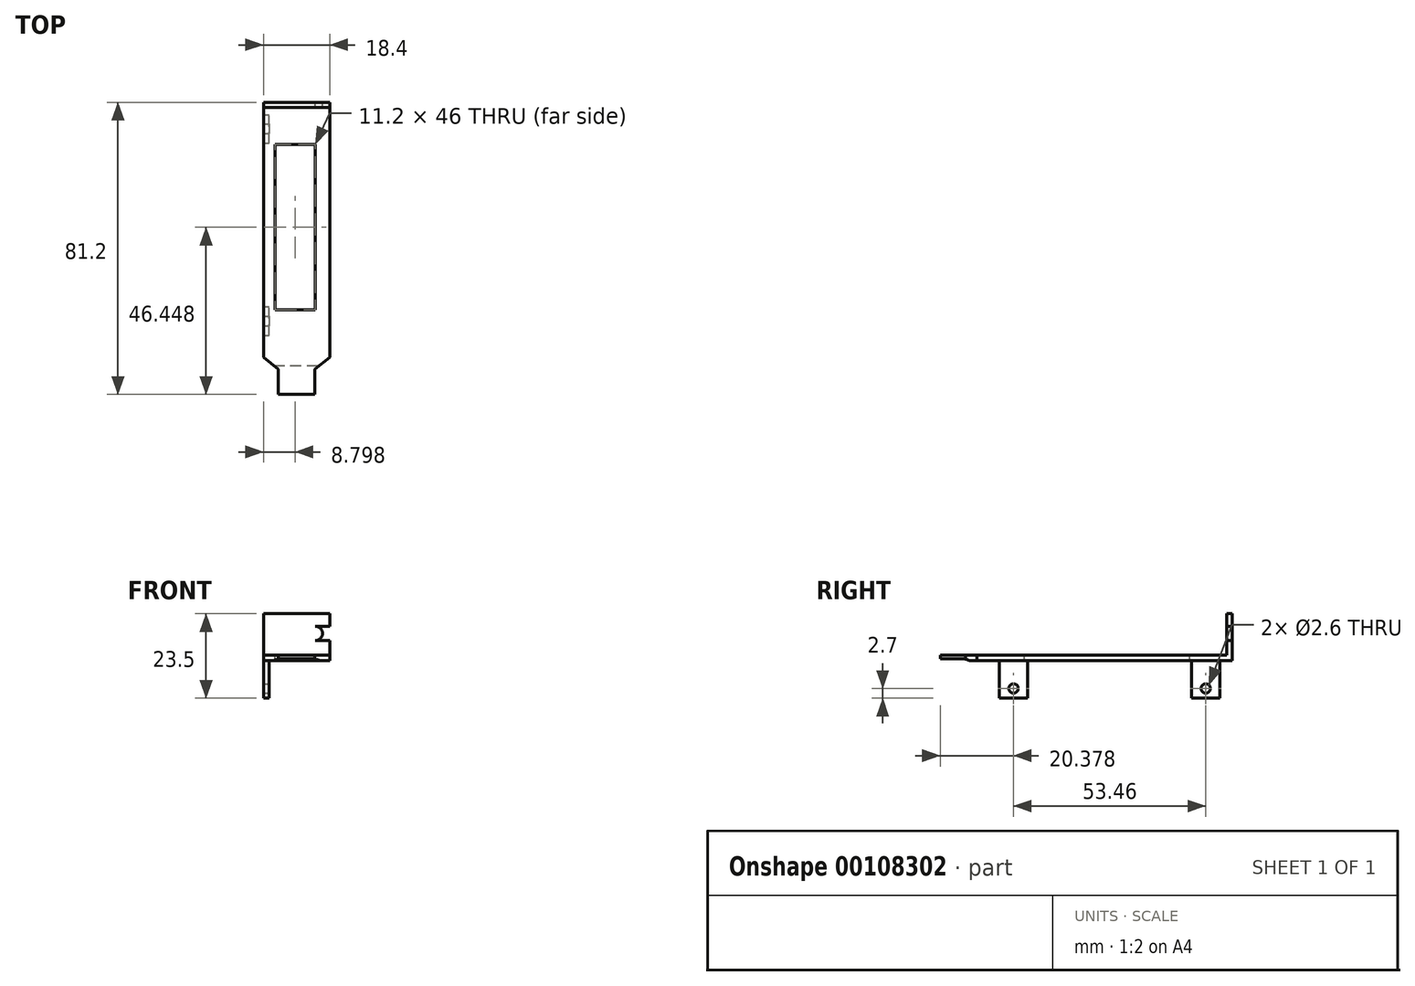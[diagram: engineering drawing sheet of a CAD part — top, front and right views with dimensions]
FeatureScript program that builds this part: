
annotation { "Feature Type Name" : "Feature", "Feature Type Description" : "" }
export const myFeature = defineFeature(function(context is Context, id is Id, definition is map)
    precondition{}
    {
        {
            var Q0;
            Q0=qCreatedBy(makeId("Top.planeOp"),FACE);
            var sketch = newSketch(context, id + "F0", { "sketchPlane" : qUnion([Q0])});
            skLineSegment(sketch, "E0.bottom", {"start": v(-5.44, 44.64) * mm, "end": v(12.96, 44.64) * mm});
            skLineSegment(sketch, "E0.left", {"start": v(-5.44, 44.64) * mm, "end": v(-5.44, -26.3) * mm});
            skLineSegment(sketch, "E0.right", {"start": v(12.96, 44.64) * mm, "end": v(12.96, -26.3) * mm});
            skPoint(sketch, "E0.middle", {"position": v(0, 0) * mm});
            skLineSegment(sketch, "E1", {"start": v(-1.34, -29.56) * mm, "end": v(-5.44, -26.3) * mm});
            skLineSegment(sketch, "E2", {"start": v(12.96, -26.3) * mm, "end": v(8.86, -29.56) * mm});
            skLineSegment(sketch, "E3", {"start": v(-1.34, -29.56) * mm, "end": v(8.86, -29.56) * mm});
            skLineSegment(sketch, "E4", {"start": v(-1.34, -29.56) * mm, "end": v(-1.34, -36.56) * mm});
            skLineSegment(sketch, "E5", {"start": v(-1.34, -36.56) * mm, "end": v(8.86, -36.56) * mm});
            skLineSegment(sketch, "E6", {"start": v(8.86, -36.56) * mm, "end": v(8.86, -29.56) * mm});
            skPoint(sketch, "E7.middle", {"position": v(4.18, 5.9) * mm});
            skSolve(sketch);
        }
        {
            var Q0;
            Q0 = qSketchRegion(id + "F0", true);
            extrude(context, id + "F1", {"entities" : qUnion([Q0]), "depth" : 1.5 * mm});
        }
        {
            var Q0;
            Q0=makeQuery(id+"F1.opExtrude","CAP_FACE",FACE,{"disambiguationData":[OSD([sQuery(id+"F0.wireOp",EDGE,"E0.bottom"),sQuery(id+"F0.wireOp",EDGE,"E0.left"),sQuery(id+"F0.wireOp",EDGE,"E0.right"),sQuery(id+"F0.wireOp",EDGE,"E1"),sQuery(id+"F0.wireOp",EDGE,"E2"),sQuery(id+"F0.wireOp",EDGE,"E4"),sQuery(id+"F0.wireOp",EDGE,"E5"),sQuery(id+"F0.wireOp",EDGE,"E6")])],"isStart":false});
            var sketch = newSketch(context, id + "F2", { "sketchPlane" : qUnion([Q0])});
            skLineSegment(sketch, "E8", {"start": v(-2.24, 32.89) * mm, "end": v(-2.24, -13.11) * mm});
            skLineSegment(sketch, "E9", {"start": v(-2.24, -13.11) * mm, "end": v(8.96, -13.11) * mm});
            skLineSegment(sketch, "E10", {"start": v(8.96, -13.11) * mm, "end": v(8.96, 32.89) * mm});
            skLineSegment(sketch, "E11", {"start": v(8.96, 32.89) * mm, "end": v(-2.24, 32.89) * mm});
            skLineSegment(sketch, "E12.0", {"start": v(-5.44, 44.64) * mm, "end": v(-5.44, -26.3) * mm});
            skSolve(sketch);
        }
        {
            var Q0;
            Q0=makeQuery(id+"F2.imprint","IMPRINT",FACE,{"disambiguationData":[TD([[makeQuery(id+"F2.imprint","IMPRINT",EDGE,{"derivedFrom":sQuery(id+"F2.wireOp",EDGE,"E8")}),1.0]])]});
            extrude(context, id + "F3", {"entities" : qUnion([Q0]), "operationType" : NewBodyOperationType.REMOVE, "oppositeDirection" : true, "depth" : 25 * mm});
        }
        {
            var Q0;
            Q0=makeQuery(id+"F1.opExtrude","CAP_FACE",FACE,{"disambiguationData":[OSD([sQuery(id+"F0.wireOp",EDGE,"E0.bottom"),sQuery(id+"F0.wireOp",EDGE,"E0.left"),sQuery(id+"F0.wireOp",EDGE,"E0.right"),sQuery(id+"F0.wireOp",EDGE,"E1"),sQuery(id+"F0.wireOp",EDGE,"E2"),sQuery(id+"F0.wireOp",EDGE,"E4"),sQuery(id+"F0.wireOp",EDGE,"E5"),sQuery(id+"F0.wireOp",EDGE,"E6")])],"isStart":true});
            var sketch = newSketch(context, id + "F4", { "sketchPlane" : qUnion([Q0])});
            skLineSegment(sketch, "E13", {"start": v(-3.94, 26.3) * mm, "end": v(-3.94, -44.64) * mm});
            skLineSegment(sketch, "E14", {"start": v(-3.94, 26.3) * mm, "end": v(-5.44, 26.3) * mm});
            skPoint(sketch, "E15.0", {"position": v(-5.44, -44.64) * mm});
            skLineSegment(sketch, "E16.0", {"start": v(-5.44, -44.64) * mm, "end": v(-5.44, 26.3) * mm});
            skLineSegment(sketch, "E17", {"start": v(-3.94, -44.64) * mm, "end": v(-5.44, -44.64) * mm});
            skLineSegment(sketch, "E18", {"start": v(-5.44, 26.3) * mm, "end": v(-3.94, 26.3) * mm});
            skSolve(sketch);
        }
        {
            var Q0;
            Q0=makeQuery(id+"F4.imprint","IMPRINT",FACE,{"disambiguationData":[TD([[makeQuery(id+"F4.imprint","IMPRINT",EDGE,{"derivedFrom":sQuery(id+"F4.wireOp",EDGE,"E13")}),-1.0]])]});
            extrude(context, id + "F5", {"entities" : qUnion([Q0]), "operationType" : NewBodyOperationType.ADD, "depth" : 10.5 * mm});
        }
        {
            var Q0;
            Q0=makeQuery(id+"F5.opExtrude","SWEPT_FACE",FACE,{"disambiguationData":[OSD([sQuery(id+"F4.wireOp",EDGE,"E13")])]});
            var sketch = newSketch(context, id + "F6", { "sketchPlane" : qUnion([Q0])});
            skCircle(sketch, "E19", {"center": v(-16.18, -7.8) * mm, "radius": 1.3 * mm});
            skCircle(sketch, "E20", {"center": v(37.28, -7.8) * mm, "radius": 1.3 * mm});
            skLineSegment(sketch, "E21", {"start": v(-16.18, -7.8) * mm, "end": v(37.28, -7.8) * mm, "construction": true});
            skLineSegment(sketch, "E22", {"start": v(-20.15, -10.5) * mm, "end": v(-20.15, 0) * mm});
            skLineSegment(sketch, "E23", {"start": v(-20.15, -10.5) * mm, "end": v(-12.21, -10.5) * mm});
            skLineSegment(sketch, "E24", {"start": v(-12.21, 0) * mm, "end": v(-12.21, -10.5) * mm});
            skLineSegment(sketch, "E25", {"start": v(33.3, -10.5) * mm, "end": v(33.3, 0) * mm});
            skLineSegment(sketch, "E26", {"start": v(33.3, -10.5) * mm, "end": v(41.2, -10.5) * mm});
            skLineSegment(sketch, "E27", {"start": v(41.2, 0) * mm, "end": v(41.2, -10.5) * mm});
            skSolve(sketch);
        }
        {
            var Q0;
            {var subQ0=sQuery(id+"F6.wireOp",EDGE,"E24");Q0=makeQuery(id+"F6.imprint","IMPRINT",FACE,{"disambiguationData":[TD([[makeQuery(id+"F6.imprint","IMPRINT",EDGE,{"derivedFrom":subQ0}),1.0]])]});}
            var Q1;
            Q1=makeQuery(id+"F6.imprint","IMPRINT",FACE,{"disambiguationData":[TD([[makeQuery(id+"F6.imprint","IMPRINT",EDGE,{"derivedFrom":sQuery(id+"F6.wireOp",EDGE,"E19")}),1.0]])]});
            var Q2;
            Q2=makeQuery(id+"F6.imprint","IMPRINT",FACE,{"disambiguationData":[TD([[makeQuery(id+"F6.imprint","IMPRINT",EDGE,{"derivedFrom":sQuery(id+"F6.wireOp",EDGE,"E20")}),1.0]])]});
            var Q3;
            {var subQ3=sQuery(id+"F6.wireOp",EDGE,"E27");Q3=makeQuery(id+"F6.imprint","IMPRINT",FACE,{"disambiguationData":[TD([[makeQuery(id+"F6.imprint","IMPRINT",EDGE,{"derivedFrom":subQ3}),1.0]])]});}
            var Q4;
            {var subQ0=sQuery(id+"F6.wireOp",EDGE,"E22");Q4=makeQuery(id+"F6.imprint","IMPRINT",FACE,{"disambiguationData":[TD([[makeQuery(id+"F6.imprint","IMPRINT",EDGE,{"derivedFrom":subQ0}),1.0]])]});}
            extrude(context, id + "F7", {"entities" : qUnion([Q0, Q1, Q2, Q3, Q4]), "operationType" : NewBodyOperationType.REMOVE, "oppositeDirection" : true, "depth" : 25 * mm});
        }
        {
            var Q0;
            {var subQ0=sQuery(id+"F4.wireOp",EDGE,"E13");var subQ1=makeQuery(id+"F5.opExtrude","CAP_EDGE",EDGE,{"disambiguationData":[OSD([subQ0])],"isStart":true});var subQ2=sQuery(id+"F0.wireOp",EDGE,"E0.bottom");Q0=makeQuery(id+"F7.boolean.opBoolean","MERGE",FACE,{"derivedFrom":[makeQuery(id+"F1.opExtrude","CAP_FACE",FACE,{"disambiguationData":[OSD([subQ2,sQuery(id+"F0.wireOp",EDGE,"E0.left"),sQuery(id+"F0.wireOp",EDGE,"E0.right"),sQuery(id+"F0.wireOp",EDGE,"E1"),sQuery(id+"F0.wireOp",EDGE,"E2"),sQuery(id+"F0.wireOp",EDGE,"E4"),sQuery(id+"F0.wireOp",EDGE,"E5"),sQuery(id+"F0.wireOp",EDGE,"E6")])],"isStart":true}),makeQuery(id+"F7.opExtrude","SWEPT_FACE",FACE,{"disambiguationData":[OSD([subQ0]),TDD([makeQuery(id+"F6.imprint","IMPRINT",EDGE,{"disambiguationData":[TD([[makeQuery(id+"F6.imprint","INTERSECT",VERTEX,{"derivedFrom":[subQ1,sQuery(id+"F6.wireOp",EDGE,"E22")]}),1.0]])],"derivedFrom":subQ1})])]}),makeQuery(id+"F7.opExtrude","SWEPT_FACE",FACE,{"disambiguationData":[OSD([subQ0]),TDD([makeQuery(id+"F6.imprint","IMPRINT",EDGE,{"disambiguationData":[TD([[makeQuery(id+"F6.imprint","INTERSECT",VERTEX,{"derivedFrom":[subQ1,sQuery(id+"F6.wireOp",EDGE,"E27")]}),-1.0]])],"derivedFrom":subQ1})])]}),makeQuery(id+"F7.opExtrude","SWEPT_FACE",FACE,{"disambiguationData":[OSD([subQ0]),TDD([makeQuery(id+"F6.imprint","IMPRINT",EDGE,{"disambiguationData":[TD([[makeQuery(id+"F6.imprint","INTERSECT",VERTEX,{"derivedFrom":[subQ1,sQuery(id+"F6.wireOp",EDGE,"E24")]}),-1.0]])],"derivedFrom":subQ1})])]})]});}
            var sketch = newSketch(context, id + "F8", { "sketchPlane" : qUnion([Q0])});
            skLineSegment(sketch, "E28", {"start": v(-2.6, 28.56) * mm, "end": v(10.11, 28.56) * mm});
            skSolve(sketch);
        }
        {
            var Q0;
            {var subQ0=sQuery(id+"F8.wireOp",EDGE,"E28");Q0=makeQuery(id+"F8.imprint","IMPRINT",FACE,{"disambiguationData":[TD([[makeQuery(id+"F8.imprint","IMPRINT",EDGE,{"derivedFrom":subQ0}),1.0]])]});}
            extrude(context, id + "F9", {"entities" : qUnion([Q0]), "operationType" : NewBodyOperationType.REMOVE, "oppositeDirection" : true, "depth" : .50 * mm});
        }
        {
            var Q0;
            Q0=makeQuery(id+"F9.boolean.opBoolean","COPY",EDGE,{"derivedFrom":makeQuery(id+"F9.opExtrude","CAP_EDGE",EDGE,{"disambiguationData":[OSD([sQuery(id+"F8.wireOp",EDGE,"E28")])],"isStart":false})});
            fillet(context, id + "F10", {"entities" : qUnion([Q0]), "radius" : 5 * mm, "tangentPropagation" : true, "allowEdgeOverflow" : false});
        }
        {
            var Q0;
            Q0=makeQuery(id+"F1.opExtrude","CAP_FACE",FACE,{"disambiguationData":[OSD([sQuery(id+"F0.wireOp",EDGE,"E0.bottom"),sQuery(id+"F0.wireOp",EDGE,"E0.left"),sQuery(id+"F0.wireOp",EDGE,"E0.right"),sQuery(id+"F0.wireOp",EDGE,"E1"),sQuery(id+"F0.wireOp",EDGE,"E2"),sQuery(id+"F0.wireOp",EDGE,"E4"),sQuery(id+"F0.wireOp",EDGE,"E5"),sQuery(id+"F0.wireOp",EDGE,"E6")])],"isStart":false});
            var sketch = newSketch(context, id + "F11", { "sketchPlane" : qUnion([Q0])});
            skLineSegment(sketch, "E29", {"start": v(-5.44, 43.14) * mm, "end": v(12.96, 43.14) * mm});
            skSolve(sketch);
        }
        {
            var Q0;
            {var subQ0=sQuery(id+"F11.wireOp",EDGE,"E29");Q0=makeQuery(id+"F11.imprint","IMPRINT",FACE,{"disambiguationData":[TD([[makeQuery(id+"F11.imprint","IMPRINT",EDGE,{"derivedFrom":subQ0}),1.0]])]});}
            extrude(context, id + "F12", {"entities" : qUnion([Q0]), "operationType" : NewBodyOperationType.ADD, "depth" : 11.5 * mm});
        }
        {
            var Q0;
            {var subQ0=sQuery(id+"F0.wireOp",EDGE,"E0.bottom");Q0=makeQuery(id+"F12.boolean.opBoolean","MERGE",FACE,{"derivedFrom":[makeQuery(id+"F1.opExtrude","SWEPT_FACE",FACE,{"disambiguationData":[OSD([subQ0])]}),makeQuery(id+"F12.opExtrude","SWEPT_FACE",FACE,{"disambiguationData":[OSD([subQ0])]})]});}
            var sketch = newSketch(context, id + "F13", { "sketchPlane" : qUnion([Q0])});
            skLineSegment(sketch, "E30.0", {"start": v(5.44, 13) * mm, "end": v(5.44, 0) * mm});
            skLineSegment(sketch, "E30.1", {"start": v(5.44, 0) * mm, "end": v(-12.96, 0) * mm});
            skLineSegment(sketch, "E31.0", {"start": v(5.44, 13) * mm, "end": v(-12.96, 13) * mm});
            skLineSegment(sketch, "E32.0", {"start": v(5.44, 1.5) * mm, "end": v(-12.96, 1.5) * mm});
            skLineSegment(sketch, "E33", {"start": v(-3.76, 0) * mm, "end": v(-3.76, 13) * mm, "construction": true});
            skLineSegment(sketch, "E34.MirrorCS", {"start": v(-8.96, 5.5) * mm, "end": v(-12.96, 5.5) * mm});
            skLineSegment(sketch, "E35.MirrorCS", {"start": v(-8.96, 9.5) * mm, "end": v(-12.96, 9.5) * mm});
            skCircle(sketch, "E36.MirrorC", {"center": v(-8.96, 7.5) * mm, "radius": 2 * mm});
            skSolve(sketch);
        }
        {
            var Q0;
            {var subQ0=sQuery(id+"F13.wireOp",EDGE,"E36.MirrorC");var subQ1=makeQuery(id+"F13.imprint","INTERSECT",VERTEX,{"derivedFrom":[sQuery(id+"F13.wireOp",EDGE,"E34.MirrorCS"),subQ0]});Q0=makeQuery(id+"F13.imprint","IMPRINT",FACE,{"disambiguationData":[TD([[makeQuery(id+"F13.imprint","IMPRINT",EDGE,{"disambiguationData":[TD([[subQ1,1.0]])],"derivedFrom":subQ0}),-1.0]])]});}
            var Q1;
            {var subQ0=sQuery(id+"F13.wireOp",EDGE,"E34.MirrorCS");Q1=makeQuery(id+"F13.imprint","IMPRINT",FACE,{"disambiguationData":[TD([[makeQuery(id+"F13.imprint","IMPRINT",EDGE,{"derivedFrom":subQ0}),-1.0]])]});}
            var Q2;
            Q2=makeQuery(id+"F12.opExtrude","SWEPT_FACE",FACE,{"disambiguationData":[OSD([sQuery(id+"F11.wireOp",EDGE,"E29")])]});
            extrude(context, id + "F14", {"entities" : qUnion([Q0, Q1]), "operationType" : NewBodyOperationType.REMOVE, "endBound" : BoundingType.UP_TO_SURFACE, "oppositeDirection" : true, "endBoundEntityFace" : qUnion([Q2]), "depth" : 25 * mm});
        }
    });
